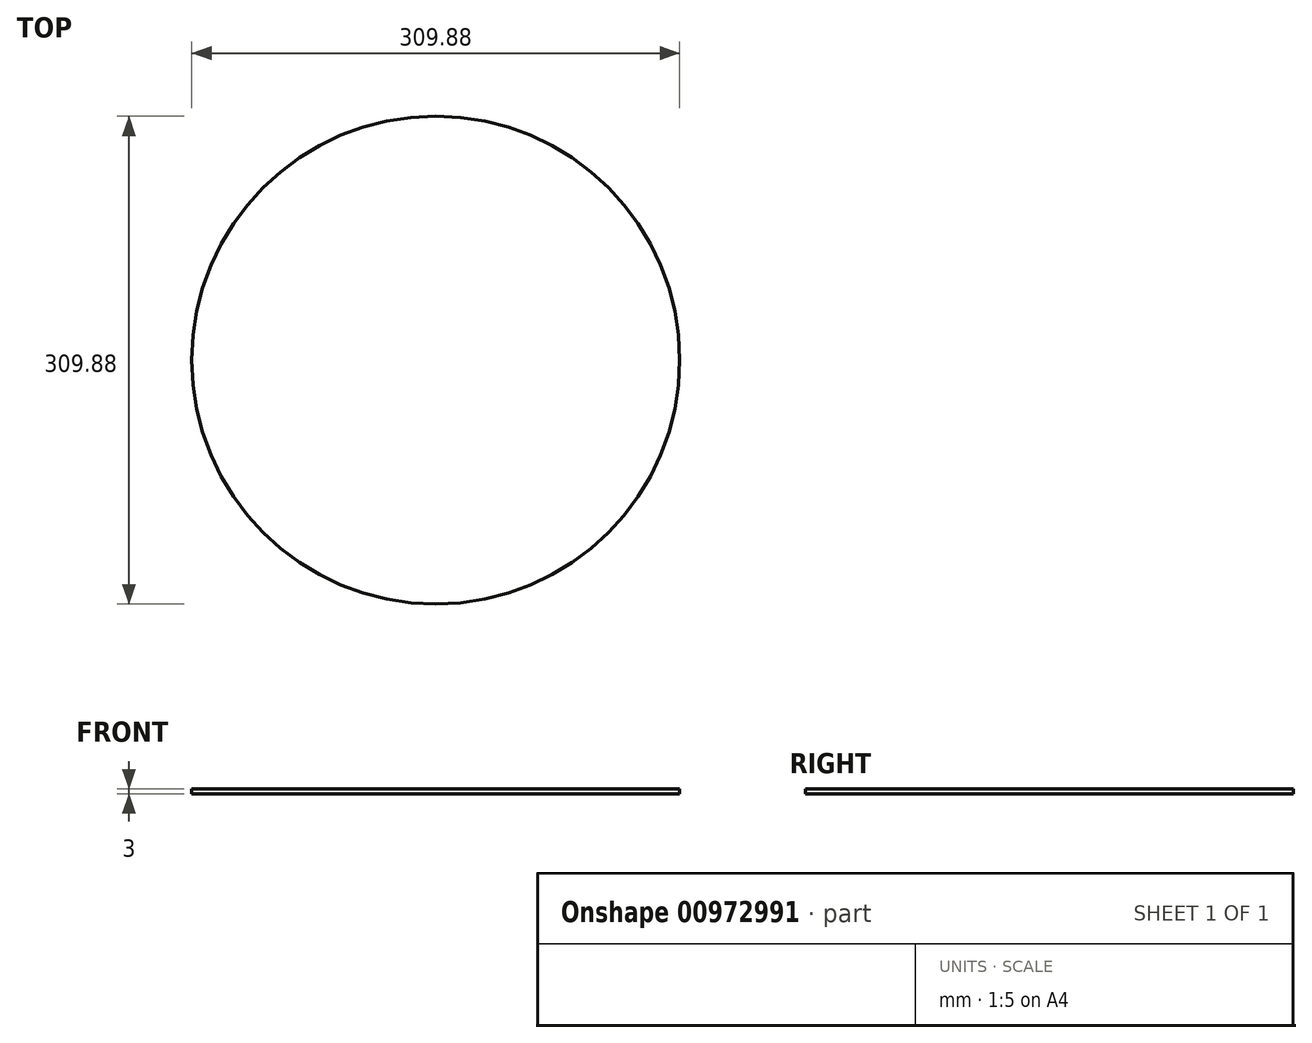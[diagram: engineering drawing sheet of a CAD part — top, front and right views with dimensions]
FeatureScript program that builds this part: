
annotation { "Feature Type Name" : "Feature", "Feature Type Description" : "" }
export const myFeature = defineFeature(function(context is Context, id is Id, definition is map)
    precondition{}
    {
        {
            var Q0;
            Q0=qCreatedBy(makeId("Top.planeOp"),FACE);
            var sketch = newSketch(context, id + "F0", { "sketchPlane" : qUnion([Q0])});
            skCircle(sketch, "E0", {"center": v(0, 0) * mm, "radius": 154.94 * mm});
            skSolve(sketch);
        }
        {
            var Q0;
            Q0 = qSketchRegion(id + "F0", true);
            extrude(context, id + "F1", {"entities" : qUnion([Q0]), "depth" : 3 * mm, "offsetDistance" : 25 * mm});
        }
    });
